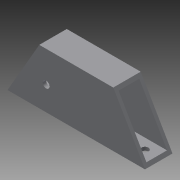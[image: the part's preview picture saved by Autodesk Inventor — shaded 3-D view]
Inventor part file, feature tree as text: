
AUTODESK INVENTOR PART (.ipt)
format: ipt  version: 2013 (Build 170138000, 138)  size: 112,640 bytes
history: native  units: in
note: dims shown in document units (in); Inventor stores cm internally (conversion verified against a paired STEP export)
features: extrude x5, sketch x5
ambient origin geometry x8: Origin, YZ Plane, XZ Plane, XY Plane, X Axis, Y Axis, Z Axis, Center Point
bodies: Solid1 (feature_tree)
feature tree (10):
  extrude  "Extrusion1"  Depth=2.0in
  extrude  "Extrusion2"  Depth=0.75in
  extrude  "Extrusion3"  Depth=99.0in TaperAngle=0.0deg
  extrude  "Extrusion4"  TaperAngle=120.0deg  [1 undecoded]
  extrude  "Extrusion5"  Depth=0.25in
  sketch  "Sketch1"  dims[d0=5.0in d1=2.0in]
  sketch  "Sketch2"  dims[d2=1.0in d3=0.0in d4=0.75in]
  sketch  "Sketch3"  dims[d5=1.75in d6=99.0in d7=0.0in]
  sketch  "Sketch4"  dims[d8=60.0deg d9=120.0deg]
  sketch  "Sketch5"  dims[d10=99.0in d11=0.0in d12=0.25in d13=0.25in d14=99.0in d15=0.0in d16=0.25in d17=0.8755in d18=90.0deg d19=0.5in d20=0.25in d21=99.0in d22=0.0in]
note: 1 required parameter value undecoded (feature->parameter linkage not recoverable at this tier; creation-order binding heuristic only, values carry confidence <= 0.55)
